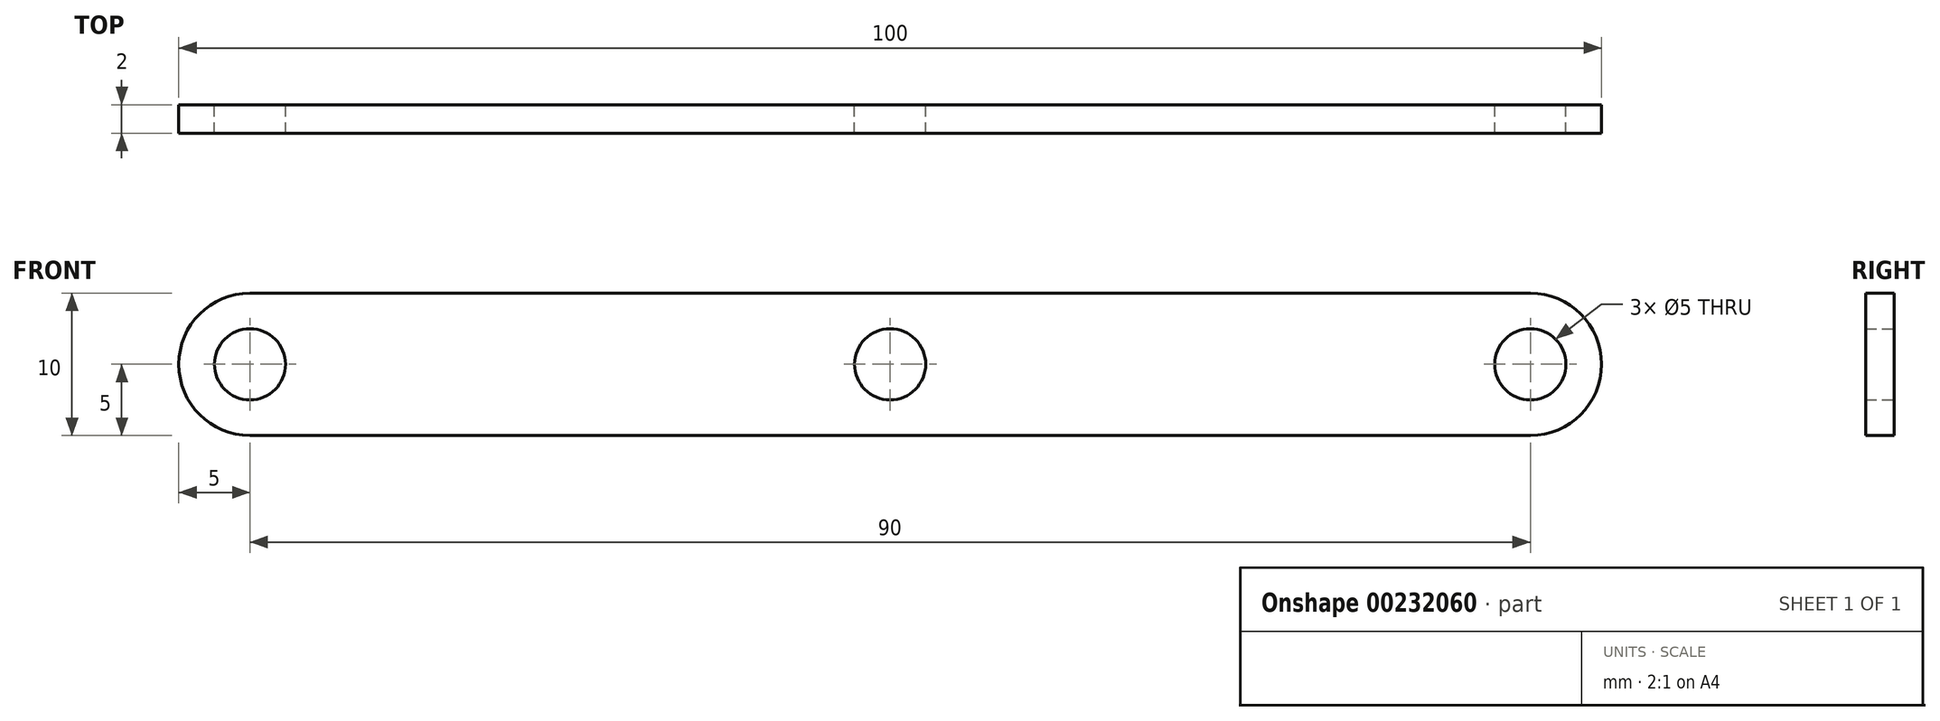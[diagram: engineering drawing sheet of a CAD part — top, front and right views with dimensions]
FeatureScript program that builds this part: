
annotation { "Feature Type Name" : "Feature", "Feature Type Description" : "" }
export const myFeature = defineFeature(function(context is Context, id is Id, definition is map)
    precondition{}
    {
        {
            var Q0;
            Q0=qCreatedBy(makeId("Front.planeOp"),FACE);
            var sketch = newSketch(context, id + "F0", { "sketchPlane" : qUnion([Q0])});
            skLineSegment(sketch, "E0.bottom", {"start": v(-50, 5) * mm, "end": v(50, 5) * mm});
            skLineSegment(sketch, "E0.top", {"start": v(-50, -5) * mm, "end": v(50, -5) * mm});
            skLineSegment(sketch, "E0.left", {"start": v(-50, 5) * mm, "end": v(-50, -5) * mm});
            skLineSegment(sketch, "E0.right", {"start": v(50, 5) * mm, "end": v(50, -5) * mm});
            skCircle(sketch, "E1", {"center": v(0, 0) * mm, "radius": 2.5 * mm});
            skCircle(sketch, "E2", {"center": v(45, 0) * mm, "radius": 2.5 * mm});
            skPoint(sketch, "E2.centerSnap0", {"position": v(50, 0) * mm});
            skCircle(sketch, "E3", {"center": v(-45, 0) * mm, "radius": 2.5 * mm});
            skPoint(sketch, "E3.centerSnap0", {"position": v(-50, 0) * mm});
            skSolve(sketch);
        }
        {
            var Q0;
            Q0=makeQuery(id+"F0.imprint","IMPRINT",FACE,{"disambiguationData":[TD([[makeQuery(id+"F0.imprint","IMPRINT",EDGE,{"derivedFrom":sQuery(id+"F0.wireOp",EDGE,"E0.bottom")}),-1.0]])]});
            extrude(context, id + "F1", {"entities" : qUnion([Q0]), "depth" : 2 * mm});
        }
        {
            var Q0;
            Q0=makeQuery(id+"F1.opExtrude","SWEPT_EDGE",EDGE,{"disambiguationData":[OSD([sQuery(id+"F0.wireOp",EDGE,"E0.bottom"),sQuery(id+"F0.wireOp",EDGE,"E0.left")])]});
            var Q1;
            Q1=makeQuery(id+"F1.opExtrude","SWEPT_EDGE",EDGE,{"disambiguationData":[OSD([sQuery(id+"F0.wireOp",EDGE,"E0.top"),sQuery(id+"F0.wireOp",EDGE,"E0.left")])]});
            var Q2;
            Q2=makeQuery(id+"F1.opExtrude","SWEPT_EDGE",EDGE,{"disambiguationData":[OSD([sQuery(id+"F0.wireOp",EDGE,"E0.top"),sQuery(id+"F0.wireOp",EDGE,"E0.right")])]});
            var Q3;
            Q3=makeQuery(id+"F1.opExtrude","SWEPT_EDGE",EDGE,{"disambiguationData":[OSD([sQuery(id+"F0.wireOp",EDGE,"E0.bottom"),sQuery(id+"F0.wireOp",EDGE,"E0.right")])]});
            fillet(context, id + "F2", {"entities" : qUnion([Q0, Q1, Q2, Q3]), "radius" : 5 * mm, "tangentPropagation" : true, "allowEdgeOverflow" : false});
        }
        {
            var Q0;
            Q0=makeQuery(id+"F1.opExtrude","SWEPT_BODY",BODY,{"disambiguationData":[OSD([sQuery(id+"F0.wireOp",EDGE,"E0.bottom"),sQuery(id+"F0.wireOp",EDGE,"E0.top"),sQuery(id+"F0.wireOp",EDGE,"E0.left"),sQuery(id+"F0.wireOp",EDGE,"E0.right"),sQuery(id+"F0.wireOp",EDGE,"E1"),sQuery(id+"F0.wireOp",EDGE,"E2"),sQuery(id+"F0.wireOp",EDGE,"E3")])]});
            transform(context, id + "F3", {"entities" : qUnion([Q0]), "transformType" : TransformType.TRANSLATION_3D, "dx" : 0 * mm, "dy" : -2 * mm, "dz" : 0 * mm, "makeCopy" : true});
        }
        {
            var Q0;
            Q0=makeQuery(id+"F3.opPattern","COPY",BODY,{"derivedFrom":makeQuery(id+"F1.opExtrude","SWEPT_BODY",BODY,{"disambiguationData":[OSD([sQuery(id+"F0.wireOp",EDGE,"E0.bottom"),sQuery(id+"F0.wireOp",EDGE,"E0.top"),sQuery(id+"F0.wireOp",EDGE,"E0.left"),sQuery(id+"F0.wireOp",EDGE,"E0.right"),sQuery(id+"F0.wireOp",EDGE,"E1"),sQuery(id+"F0.wireOp",EDGE,"E2"),sQuery(id+"F0.wireOp",EDGE,"E3")])]}),"instanceName":"1"});
            deleteBodies(context, id + "F4", {"entities" : qUnion([Q0])});
        }
    });
